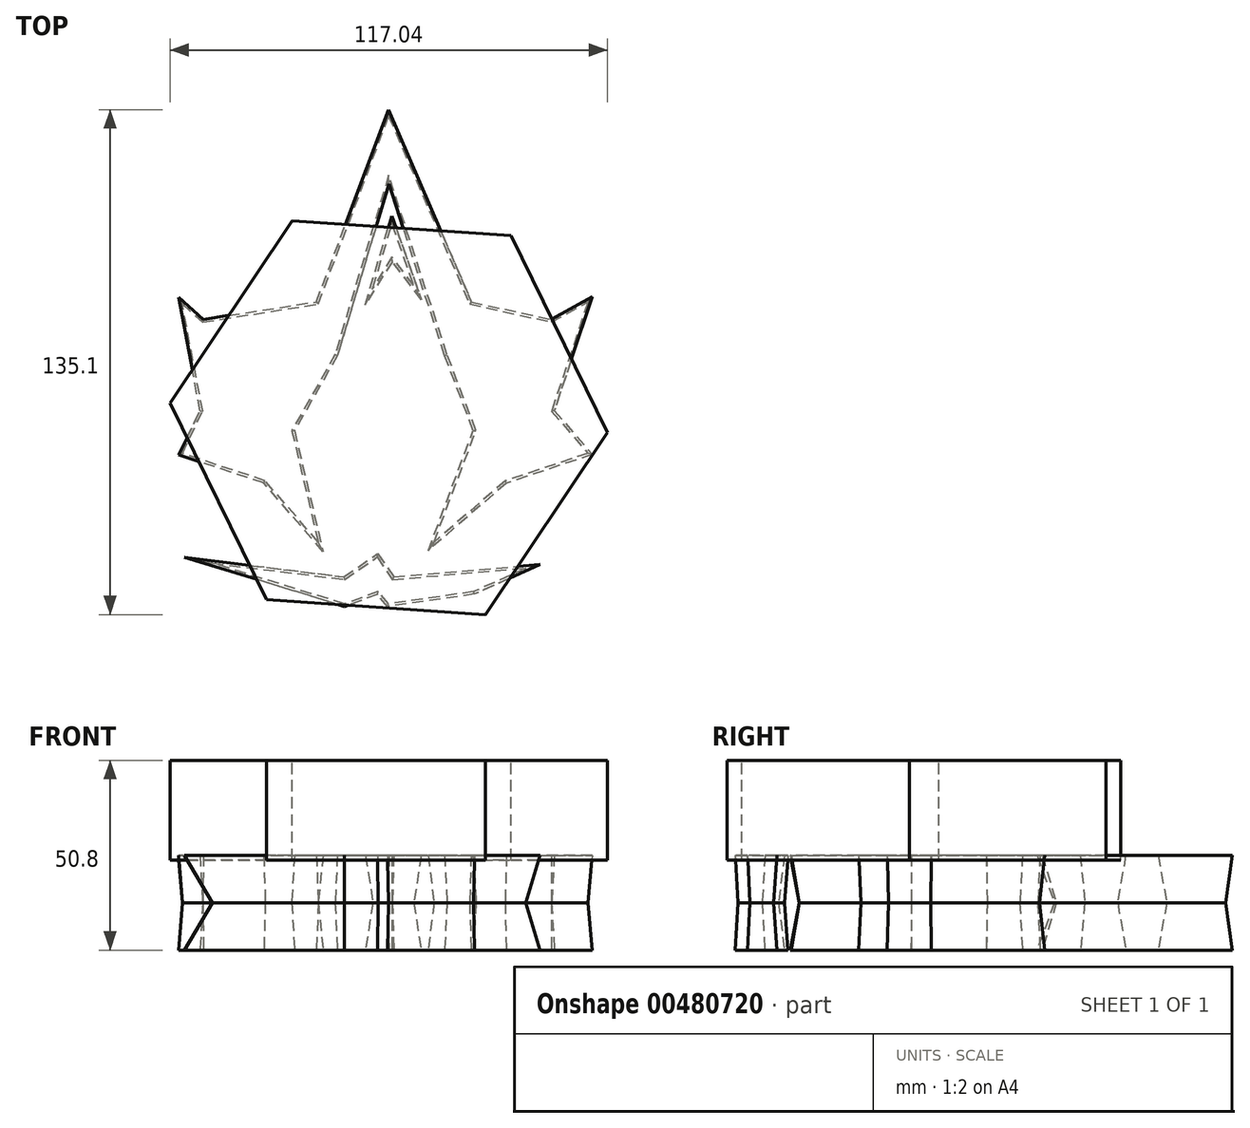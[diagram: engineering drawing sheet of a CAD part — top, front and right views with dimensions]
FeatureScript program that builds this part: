
annotation { "Feature Type Name" : "Feature", "Feature Type Description" : "" }
export const myFeature = defineFeature(function(context is Context, id is Id, definition is map)
    precondition{}
    {
        {
            var Q0;
            Q0=qCreatedBy(makeId("Top.planeOp"),FACE);
            var sketch = newSketch(context, id + "F0", { "sketchPlane" : qUnion([Q0])});
            skLineSegment(sketch, "E0", {"start": v(0, 57.8) * mm, "end": v(-18.84, 7.57) * mm});
            skLineSegment(sketch, "E1", {"start": v(-18.84, 7.57) * mm, "end": v(-49.75, 2.74) * mm});
            skLineSegment(sketch, "E2", {"start": v(-49.75, 2.74) * mm, "end": v(-55.23, 7.57) * mm});
            skLineSegment(sketch, "E3", {"start": v(-55.23, 7.57) * mm, "end": v(-49.75, -21.09) * mm});
            skLineSegment(sketch, "E4", {"start": v(-49.75, -21.09) * mm, "end": v(-55.23, -32.36) * mm});
            skLineSegment(sketch, "E5", {"start": v(-55.23, -32.36) * mm, "end": v(-33, -39.76) * mm});
            skLineSegment(sketch, "E6", {"start": v(-33, -39.76) * mm, "end": v(-18.84, -56.18) * mm});
            skLineSegment(sketch, "E7", {"start": v(-18.84, -56.18) * mm, "end": v(-25.93, -26.24) * mm});
            skPoint(sketch, "E7.endSnap0", {"position": v(-25.93, -47.97) * mm});
            skLineSegment(sketch, "E8", {"start": v(-25.93, -26.24) * mm, "end": v(-14.34, -5.96) * mm});
            skLineSegment(sketch, "E9", {"start": v(-14.34, -5.96) * mm, "end": v(0, 42.02) * mm});
            skLineSegment(sketch, "E10", {"start": v(0, 42.02) * mm, "end": v(15.6, -5.96) * mm});
            skLineSegment(sketch, "E11", {"start": v(15.6, -5.96) * mm, "end": v(23.34, -26.24) * mm});
            skLineSegment(sketch, "E12", {"start": v(23.34, -26.24) * mm, "end": v(12.1, -56.18) * mm});
            skLineSegment(sketch, "E13", {"start": v(12.1, -56.18) * mm, "end": v(21.62, -47.97) * mm});
            skLineSegment(sketch, "E14", {"start": v(21.62, -47.97) * mm, "end": v(31.13, -39.76) * mm});
            skLineSegment(sketch, "E15", {"start": v(31.13, -39.76) * mm, "end": v(53.28, -32.36) * mm});
            skLineSegment(sketch, "E16", {"start": v(53.28, -32.36) * mm, "end": v(43.56, -21.09) * mm});
            skLineSegment(sketch, "E17", {"start": v(43.56, -21.09) * mm, "end": v(53.28, 8.08) * mm});
            skLineSegment(sketch, "E18", {"start": v(53.28, 8.08) * mm, "end": v(43.56, 2.74) * mm});
            skLineSegment(sketch, "E19", {"start": v(43.56, 2.74) * mm, "end": v(21.62, 7.57) * mm});
            skLineSegment(sketch, "E20", {"start": v(21.62, 7.57) * mm, "end": v(0, 57.8) * mm});
            skLineSegment(sketch, "E21", {"start": v(-47.2, -61.78) * mm, "end": v(-11.82, -66.13) * mm});
            skLineSegment(sketch, "E22", {"start": v(-11.82, -66.13) * mm, "end": v(-3.12, -60.14) * mm});
            skLineSegment(sketch, "E23", {"start": v(-3.12, -60.14) * mm, "end": v(1, -66.13) * mm});
            skLineSegment(sketch, "E24", {"start": v(1, -66.13) * mm, "end": v(36.62, -63.14) * mm});
            skPoint(sketch, "E24.endSnap0", {"position": v(-7.47, -63.14) * mm});
            skLineSegment(sketch, "E25", {"start": v(36.62, -63.14) * mm, "end": v(22.74, -69.4) * mm});
            skLineSegment(sketch, "E26", {"start": v(22.74, -69.4) * mm, "end": v(0, -72.66) * mm});
            skLineSegment(sketch, "E27", {"start": v(0, -72.66) * mm, "end": v(-2.82, -69.4) * mm});
            skLineSegment(sketch, "E28", {"start": v(-2.82, -69.4) * mm, "end": v(-11.82, -72.66) * mm});
            skLineSegment(sketch, "E29", {"start": v(-11.82, -72.66) * mm, "end": v(-47.2, -61.78) * mm});
            skLineSegment(sketch, "E30", {"start": v(-4.2, 11.97) * mm, "end": v(0.86, 28.93) * mm});
            skLineSegment(sketch, "E31", {"start": v(0.86, 28.93) * mm, "end": v(6.68, 12.52) * mm});
            skLineSegment(sketch, "E32", {"start": v(6.68, 12.52) * mm, "end": v(0.86, 20.14) * mm});
            skLineSegment(sketch, "E33", {"start": v(0.86, 20.14) * mm, "end": v(-4.2, 11.97) * mm});
            skSolve(sketch);
        }
        {
            var Q0;
            Q0 = qSketchRegion(id + "F0", true);
            extrude(context, id + "F1", {"entities" : qUnion([Q0]), "endBound" : BoundingType.SYMMETRIC, "depth" : 25.4 * mm, "hasDraft" : true, "draftAngle" : 3 * degree});
        }
        {
            var Q0;
            Q0=makeQuery(id+"F1.opExtrude","CAP_FACE",FACE,{"disambiguationData":[OSD([sQuery(id+"F0.wireOp",EDGE,"E0"),sQuery(id+"F0.wireOp",EDGE,"E1"),sQuery(id+"F0.wireOp",EDGE,"E2"),sQuery(id+"F0.wireOp",EDGE,"E3"),sQuery(id+"F0.wireOp",EDGE,"E4"),sQuery(id+"F0.wireOp",EDGE,"E5"),sQuery(id+"F0.wireOp",EDGE,"E6"),sQuery(id+"F0.wireOp",EDGE,"E7"),sQuery(id+"F0.wireOp",EDGE,"E8"),sQuery(id+"F0.wireOp",EDGE,"E9"),sQuery(id+"F0.wireOp",EDGE,"E10"),sQuery(id+"F0.wireOp",EDGE,"E11"),sQuery(id+"F0.wireOp",EDGE,"E12"),sQuery(id+"F0.wireOp",EDGE,"E13"),sQuery(id+"F0.wireOp",EDGE,"E14"),sQuery(id+"F0.wireOp",EDGE,"E15"),sQuery(id+"F0.wireOp",EDGE,"E16"),sQuery(id+"F0.wireOp",EDGE,"E17"),sQuery(id+"F0.wireOp",EDGE,"E18"),sQuery(id+"F0.wireOp",EDGE,"E19"),sQuery(id+"F0.wireOp",EDGE,"E20")])],"isStart":false});
            cPlane(context, id + "F2", {"entities" : qUnion([Q0]), "cplaneType" : CPlaneType.OFFSET, "offset" : 25.4 * mm, "width" : 152.4 * mm, "height" : 152.4 * mm});
        }
        {
            var Q0;
            Q0=qCreatedBy(id+"F2.planeOp",FACE);
            var sketch = newSketch(context, id + "F3", { "sketchPlane" : qUnion([Q0])});
            skPoint(sketch, "E34.0.midPoint", {"position": v(-3, -60.42) * mm});
            skPoint(sketch, "E35.orphan", {"position": v(3.32, 33.75) * mm});
            skPoint(sketch, "E36.orphan", {"position": v(40.8, 12.5) * mm});
            skPoint(sketch, "E37.orphan", {"position": v(47.56, -30.05) * mm});
            skPoint(sketch, "E38.orphan", {"position": v(18.5, -61.86) * mm});
            skPoint(sketch, "E39.orphan", {"position": v(-24.49, -58.97) * mm});
            skPoint(sketch, "E34.cCircle.center.orphan", {"position": v(0, -15.78) * mm});
            skCircle(sketch, "E40.cCircle", {"center": v(0, -22.86) * mm, "radius": 50.8 * mm, "construction": true});
            skLineSegment(sketch, "E40.0", {"start": v(-58.52, -18.91) * mm, "end": v(-25.84, 29.8) * mm});
            skLineSegment(sketch, "E40.1", {"start": v(-25.84, 29.8) * mm, "end": v(32.68, 25.85) * mm});
            skLineSegment(sketch, "E40.2", {"start": v(32.68, 25.85) * mm, "end": v(58.52, -26.8) * mm});
            skLineSegment(sketch, "E40.3", {"start": v(58.52, -26.8) * mm, "end": v(25.84, -75.52) * mm});
            skLineSegment(sketch, "E40.4", {"start": v(25.84, -75.52) * mm, "end": v(-32.68, -71.57) * mm});
            skLineSegment(sketch, "E40.5", {"start": v(-32.68, -71.57) * mm, "end": v(-58.52, -18.91) * mm});
            skPoint(sketch, "E40.0.midPoint", {"position": v(-42.18, 5.44) * mm});
            skSolve(sketch);
        }
        {
            var Q0;
            Q0 = qSketchRegion(id + "F3", true);
            extrude(context, id + "F4", {"entities" : qUnion([Q0]), "oppositeDirection" : true, "depth" : 26.67 * mm});
        }
    });
